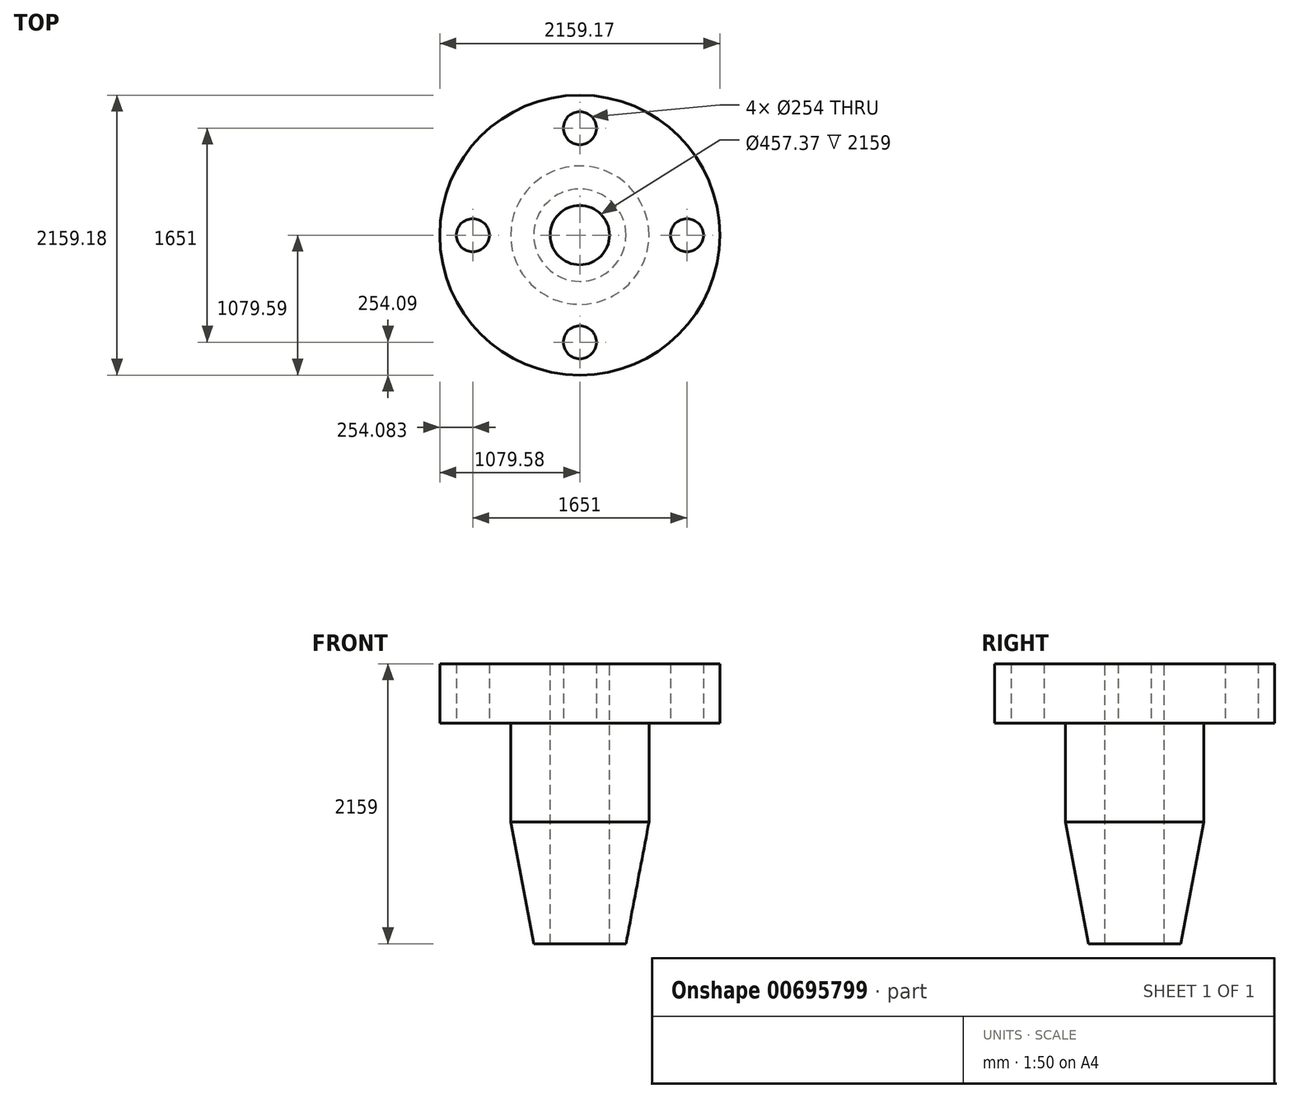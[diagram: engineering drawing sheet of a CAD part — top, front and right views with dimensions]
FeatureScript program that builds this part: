
annotation { "Feature Type Name" : "Feature", "Feature Type Description" : "" }
export const myFeature = defineFeature(function(context is Context, id is Id, definition is map)
    precondition{}
    {
        {
            var Q0;
            Q0=qCreatedBy(makeId("Front.planeOp"),FACE);
            var sketch = newSketch(context, id + "F0", { "sketchPlane" : qUnion([Q0])});
            skLineSegment(sketch, "E0", {"start": v(-19.96, -107.96) * mm, "end": v(107.04, -107.96) * mm});
            skLineSegment(sketch, "E1", {"start": v(-19.96, -107.96) * mm, "end": v(-19.96, 2051.04) * mm});
            skLineSegment(sketch, "E2", {"start": v(-19.96, 2051.04) * mm, "end": v(830.94, 2051.04) * mm});
            skLineSegment(sketch, "E3", {"start": v(830.94, 2051.04) * mm, "end": v(830.94, 1593.84) * mm});
            skLineSegment(sketch, "E4", {"start": v(830.94, 1593.84) * mm, "end": v(284.84, 1593.84) * mm});
            skLineSegment(sketch, "E5", {"start": v(284.84, 1593.84) * mm, "end": v(284.84, 831.84) * mm});
            skLineSegment(sketch, "E6", {"start": v(284.84, 831.84) * mm, "end": v(107.04, -107.96) * mm});
            skLineSegment(sketch, "E7", {"start": v(830.94, 2051.04) * mm, "end": v(-248.65, 2051.04) * mm});
            skLineSegment(sketch, "E8", {"start": v(-248.65, 2051.04) * mm, "end": v(-248.65, -405.97) * mm});
            skSolve(sketch);
        }
        {
            var Q0;
            Q0=makeQuery(id+"F0.imprint","IMPRINT",FACE,{"disambiguationData":[TD([[makeQuery(id+"F0.imprint","IMPRINT",EDGE,{"derivedFrom":sQuery(id+"F0.wireOp",EDGE,"E0")}),1.0]])]});
            var Q1;
            Q1=sQuery(id+"F0.wireOp",EDGE,"E8");
            revolve(context, id + "F1", {"entities" : qUnion([Q0]), "axis" : qUnion([Q1]), "revolveType" : RevolveType.FULL});
        }
        {
            var Q0;
            Q0=makeQuery(id+"F1.opRevolve","SWEPT_FACE",FACE,{"disambiguationData":[OSD([sQuery(id+"F0.wireOp",EDGE,"E4")])]});
            var sketch = newSketch(context, id + "F2", { "sketchPlane" : qUnion([Q0])});
            skCircle(sketch, "E9", {"center": v(-248.65, 825.5) * mm, "radius": 127 * mm});
            skCircle(sketch, "E10", {"center": v(576.85, 0) * mm, "radius": 127 * mm});
            skCircle(sketch, "E11", {"center": v(-248.65, -825.5) * mm, "radius": 127 * mm});
            skCircle(sketch, "E12", {"center": v(-1074.15, 0) * mm, "radius": 127 * mm});
            skSolve(sketch);
        }
        {
            var Q0;
            Q0=sQuery(id+"F2.wireOp",VERTEX,"E9.center");
            var Q1;
            Q1=sQuery(id+"F2.wireOp",VERTEX,"E12.center");
            var Q2;
            Q2=sQuery(id+"F2.wireOp",VERTEX,"E11.center");
            var Q3;
            Q3=sQuery(id+"F2.wireOp",VERTEX,"E10.center");
            var Q4;
            Q4=makeQuery(id+"F1.opRevolve","SWEPT_BODY",BODY,{"disambiguationData":[OSD([sQuery(id+"F0.wireOp",EDGE,"E0"),sQuery(id+"F0.wireOp",EDGE,"E1"),sQuery(id+"F0.wireOp",EDGE,"E3"),sQuery(id+"F0.wireOp",EDGE,"E4"),sQuery(id+"F0.wireOp",EDGE,"E5"),sQuery(id+"F0.wireOp",EDGE,"E6"),sQuery(id+"F0.wireOp",EDGE,"E7")])]});
            hole(context, id + "F3", {"style" : HoleStyle.SIMPLE, "endStyle" : HoleEndStyle.BLIND, "holeDiameter" : 254 * mm, "majorDiameter" : 6.35 * mm, "holeDepth" : 762 * mm, "isTappedThrough" : true, "tappedDepth" : 12.7 * mm, "tapClearance" : 3, "locations" : qUnion([Q0, Q1, Q2, Q3]), "scope" : qUnion([Q4])});
        }
    });
